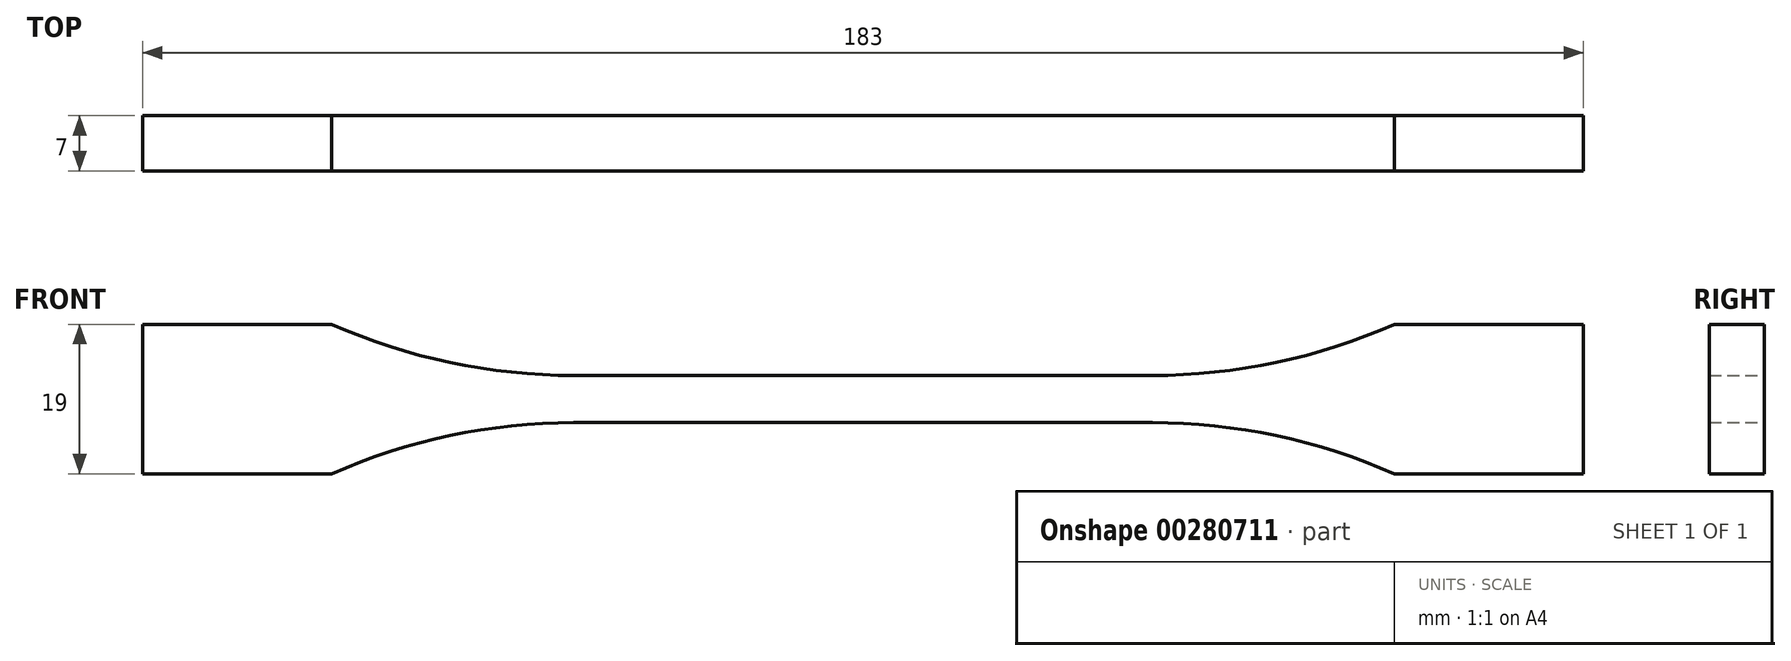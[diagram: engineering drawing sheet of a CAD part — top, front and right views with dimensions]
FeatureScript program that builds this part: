
annotation { "Feature Type Name" : "Feature", "Feature Type Description" : "" }
export const myFeature = defineFeature(function(context is Context, id is Id, definition is map)
    precondition{}
    {
        {
            var Q0;
            Q0=qCreatedBy(makeId("Front.planeOp"),FACE);
            var sketch = newSketch(context, id + "F0", { "sketchPlane" : qUnion([Q0])});
            skLineSegment(sketch, "E0", {"start": v(36.75, 3) * mm, "end": v(0, 3) * mm});
            skArc(sketch, "E1", {"start": v(36.75, 3) * mm, "mid": v(52.46, 4.64) * mm, "end": v(67.5, 9.5) * mm});
            skLineSegment(sketch, "E2", {"start": v(67.5, 9.5) * mm, "end": v(91.5, 9.5) * mm});
            skLineSegment(sketch, "E3.MirrorCS", {"start": v(67.5, -9.5) * mm, "end": v(91.5, -9.5) * mm});
            skLineSegment(sketch, "E4.MirrorCS", {"start": v(36.75, -3) * mm, "end": v(0, -3) * mm});
            skArc(sketch, "E5.MirrorCS", {"start": v(36.75, -3) * mm, "mid": v(52.46, -4.64) * mm, "end": v(67.5, -9.5) * mm});
            skLineSegment(sketch, "E6.MirrorCS", {"start": v(-36.75, 3) * mm, "end": v(0, 3) * mm});
            skLineSegment(sketch, "E7.MirrorCS", {"start": v(-67.5, 9.5) * mm, "end": v(-91.5, 9.5) * mm});
            skArc(sketch, "E8.MirrorCS", {"start": v(-36.75, -3) * mm, "mid": v(-52.46, -4.64) * mm, "end": v(-67.5, -9.5) * mm});
            skLineSegment(sketch, "E9.MirrorCS", {"start": v(-67.5, -9.5) * mm, "end": v(-91.5, -9.5) * mm});
            skLineSegment(sketch, "E10.MirrorCS", {"start": v(-36.75, -3) * mm, "end": v(0, -3) * mm});
            skArc(sketch, "E11.MirrorCS", {"start": v(-36.75, 3) * mm, "mid": v(-52.46, 4.64) * mm, "end": v(-67.5, 9.5) * mm});
            skLineSegment(sketch, "E12", {"start": v(-91.5, 9.5) * mm, "end": v(-91.5, -9.5) * mm});
            skLineSegment(sketch, "E13", {"start": v(91.5, 9.5) * mm, "end": v(91.5, -9.5) * mm});
            skSolve(sketch);
        }
        {
            var Q0;
            Q0=makeQuery(id+"F0.imprint","IMPRINT",FACE,{"disambiguationData":[TD([[makeQuery(id+"F0.imprint","IMPRINT",EDGE,{"derivedFrom":sQuery(id+"F0.wireOp",EDGE,"E0")}),1.0]])]});
            extrude(context, id + "F1", {"entities" : qUnion([Q0]), "endBound" : BoundingType.SYMMETRIC, "depth" : 7 * mm});
        }
    });
